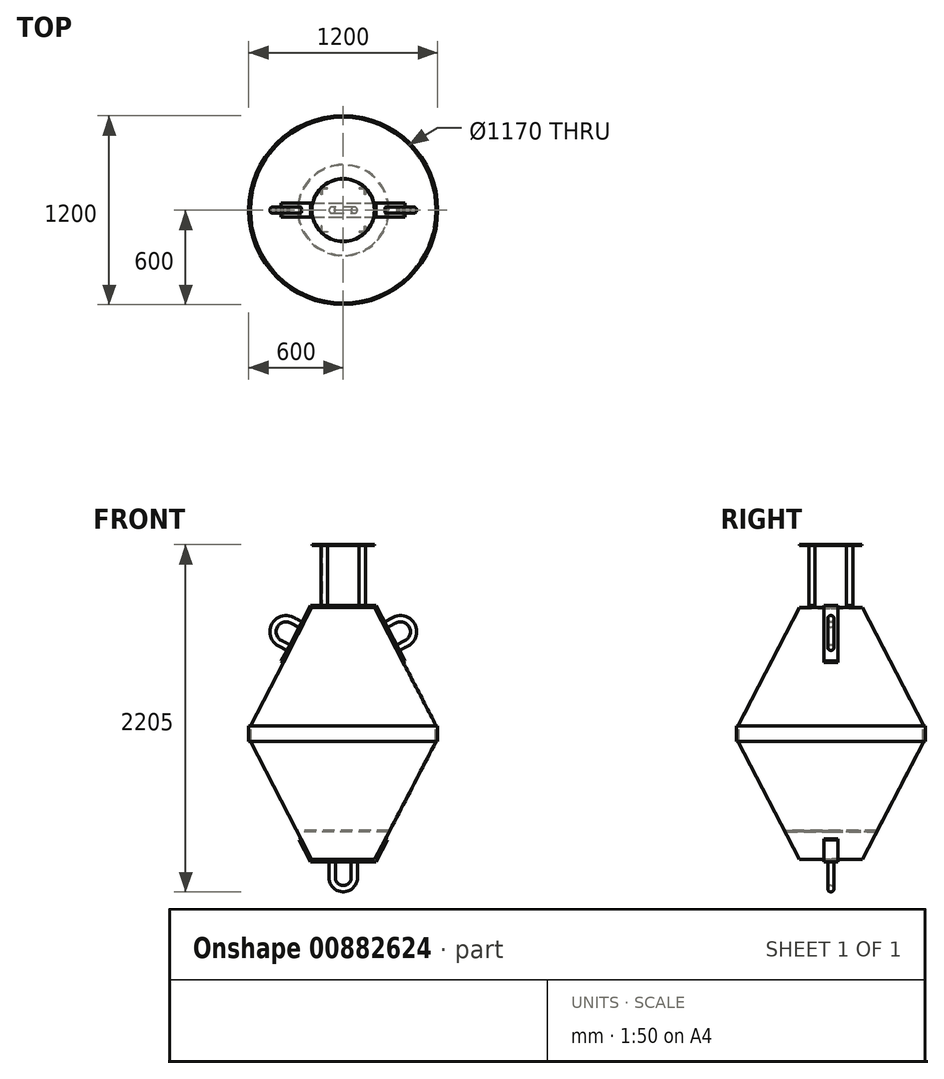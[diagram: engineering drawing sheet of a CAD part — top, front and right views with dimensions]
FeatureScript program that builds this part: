
annotation { "Feature Type Name" : "Feature", "Feature Type Description" : "" }
export const myFeature = defineFeature(function(context is Context, id is Id, definition is map)
    precondition{}
    {
        {
            var Q0;
            Q0=qCreatedBy(makeId("Front.planeOp"),FACE);
            var sketch = newSketch(context, id + "F0", { "sketchPlane" : qUnion([Q0])});
            skLineSegment(sketch, "E0", {"start": v(-100, 702.5) * mm, "end": v(290, -47.5) * mm});
            skLineSegment(sketch, "E1", {"start": v(290, -47.5) * mm, "end": v(300, -47.5) * mm});
            skLineSegment(sketch, "E2", {"start": v(300, -47.5) * mm, "end": v(300, -147.5) * mm});
            skLineSegment(sketch, "E3", {"start": v(300, -147.5) * mm, "end": v(290, -147.5) * mm});
            skLineSegment(sketch, "E4", {"start": v(290, -147.5) * mm, "end": v(-100, -897.5) * mm});
            skLineSegment(sketch, "E5", {"start": v(-100, -897.5) * mm, "end": v(-300, -897.5) * mm});
            skLineSegment(sketch, "E6", {"start": v(-300, -897.5) * mm, "end": v(-300, -892.5) * mm});
            skLineSegment(sketch, "E7", {"start": v(-300, -892.5) * mm, "end": v(-103.04, -892.5) * mm});
            skLineSegment(sketch, "E8", {"start": v(-103.04, -892.5) * mm, "end": v(-14.12, -721.5) * mm});
            skLineSegment(sketch, "E9", {"start": v(-14.12, -721.5) * mm, "end": v(-300, -721.5) * mm});
            skLineSegment(sketch, "E10", {"start": v(-300, -721.5) * mm, "end": v(-300, -713.5) * mm});
            skLineSegment(sketch, "E11", {"start": v(-300, -713.5) * mm, "end": v(-9.96, -713.5) * mm});
            skLineSegment(sketch, "E12", {"start": v(-9.96, -713.5) * mm, "end": v(285, -146.28) * mm});
            skLineSegment(sketch, "E13", {"start": v(285, -146.28) * mm, "end": v(285, -48.72) * mm});
            skLineSegment(sketch, "E14", {"start": v(285, -48.72) * mm, "end": v(-103.04, 697.5) * mm});
            skLineSegment(sketch, "E15", {"start": v(-103.04, 697.5) * mm, "end": v(-300, 697.5) * mm});
            skLineSegment(sketch, "E16", {"start": v(-300, 697.5) * mm, "end": v(-300, 702.5) * mm});
            skLineSegment(sketch, "E17", {"start": v(-300, 702.5) * mm, "end": v(-100, 702.5) * mm});
            skArc(sketch, "E18", {"start": v(-250, -1012.5) * mm, "mid": v(-264.64, -1047.86) * mm, "end": v(-300, -1062.5) * mm});
            skLineSegment(sketch, "E19", {"start": v(-300, -1062.5) * mm, "end": v(-300, -1102.5) * mm});
            skArc(sketch, "E20", {"start": v(-300, -1102.5) * mm, "mid": v(-236.36, -1076.14) * mm, "end": v(-210, -1012.5) * mm});
            skLineSegment(sketch, "E21", {"start": v(-210, -1012.5) * mm, "end": v(-210, -912.5) * mm});
            skLineSegment(sketch, "E22", {"start": v(-210, -912.5) * mm, "end": v(-250, -912.5) * mm});
            skLineSegment(sketch, "E23", {"start": v(-250, -912.5) * mm, "end": v(-250, -1012.5) * mm});
            skLineSegment(sketch, "E24", {"start": v(-300, 1102.5) * mm, "end": v(-160, 1102.5) * mm});
            skLineSegment(sketch, "E25", {"start": v(-160, 1102.5) * mm, "end": v(-160, 1097.5) * mm});
            skLineSegment(sketch, "E26", {"start": v(-160, 1097.5) * mm, "end": v(-300, 1097.5) * mm});
            skLineSegment(sketch, "E27", {"start": v(-300, 1097.5) * mm, "end": v(-300, 1102.5) * mm});
            skLineSegment(sketch, "E28", {"start": v(-200, 717.5) * mm, "end": v(-160, 717.5) * mm});
            skLineSegment(sketch, "E29", {"start": v(-160, 717.5) * mm, "end": v(-160, 1097.5) * mm});
            skLineSegment(sketch, "E30", {"start": v(-160, 1097.5) * mm, "end": v(-200, 1097.5) * mm});
            skLineSegment(sketch, "E31", {"start": v(-200, 1097.5) * mm, "end": v(-200, 717.5) * mm});
            skLineSegment(sketch, "E32", {"start": v(-90.9, 717.5) * mm, "end": v(93.65, 362.61) * mm});
            skLineSegment(sketch, "E33", {"start": v(93.65, 362.61) * mm, "end": v(80.34, 355.7) * mm});
            skLineSegment(sketch, "E34", {"start": v(80.34, 355.7) * mm, "end": v(-100, 702.5) * mm});
            skLineSegment(sketch, "E35", {"start": v(-100, 702.5) * mm, "end": v(-300, 702.5) * mm});
            skLineSegment(sketch, "E36", {"start": v(-300, 702.5) * mm, "end": v(-300, 717.5) * mm});
            skLineSegment(sketch, "E37", {"start": v(-300, 717.5) * mm, "end": v(-90.9, 717.5) * mm});
            skLineSegment(sketch, "E38", {"start": v(-17.84, -772) * mm, "end": v(-31.14, -765.08) * mm});
            skLineSegment(sketch, "E39", {"start": v(-31.14, -765.08) * mm, "end": v(-100, -897.5) * mm});
            skLineSegment(sketch, "E40", {"start": v(-300, -897.5) * mm, "end": v(-300, -912.5) * mm});
            skLineSegment(sketch, "E41", {"start": v(-300, -912.5) * mm, "end": v(-90.9, -912.5) * mm});
            skLineSegment(sketch, "E42", {"start": v(-90.9, -912.5) * mm, "end": v(-17.84, -772) * mm});
            skLineSegment(sketch, "E43", {"start": v(-18.23, 577.76) * mm, "end": v(-36.68, 613.25) * mm});
            skLineSegment(sketch, "E44", {"start": v(-36.68, 613.25) * mm, "end": v(16.55, 640.93) * mm});
            skArc(sketch, "E45", {"start": v(16.55, 640.93) * mm, "mid": v(154.78, 597.28) * mm, "end": v(111.13, 459.05) * mm});
            skLineSegment(sketch, "E46", {"start": v(111.13, 459.05) * mm, "end": v(57.9, 431.37) * mm});
            skLineSegment(sketch, "E47", {"start": v(57.9, 431.37) * mm, "end": v(39.44, 466.86) * mm});
            skLineSegment(sketch, "E48", {"start": v(39.44, 466.86) * mm, "end": v(92.67, 494.54) * mm});
            skArc(sketch, "E49", {"start": v(92.67, 494.54) * mm, "mid": v(119.29, 578.83) * mm, "end": v(35, 605.44) * mm});
            skLineSegment(sketch, "E50", {"start": v(35, 605.44) * mm, "end": v(-18.23, 577.76) * mm});
            skLineSegment(sketch, "E51", {"start": v(-300, 1102.5) * mm, "end": v(-300, -1143.28) * mm, "construction": true});
            skLineSegment(sketch, "E52.MirrorCS", {"start": v(-440, 1102.5) * mm, "end": v(-440, 1097.5) * mm});
            skLineSegment(sketch, "E53.MirrorCS", {"start": v(-440, 1097.5) * mm, "end": v(-400, 1097.5) * mm});
            skLineSegment(sketch, "E54.MirrorCS", {"start": v(-900, -147.5) * mm, "end": v(-890, -147.5) * mm});
            skLineSegment(sketch, "E55.MirrorCS", {"start": v(-500, 702.5) * mm, "end": v(-300, 702.5) * mm});
            skLineSegment(sketch, "E56.MirrorCS", {"start": v(-890, -47.5) * mm, "end": v(-900, -47.5) * mm});
            skLineSegment(sketch, "E57.MirrorCS", {"start": v(-563.32, 613.25) * mm, "end": v(-616.55, 640.93) * mm});
            skLineSegment(sketch, "E58.MirrorCS", {"start": v(-582.16, -772) * mm, "end": v(-568.86, -765.08) * mm});
            skLineSegment(sketch, "E59.MirrorCS", {"start": v(-693.65, 362.61) * mm, "end": v(-680.34, 355.7) * mm});
            skLineSegment(sketch, "E60.MirrorCS", {"start": v(-581.77, 577.76) * mm, "end": v(-563.32, 613.25) * mm});
            skLineSegment(sketch, "E61.MirrorCS", {"start": v(-635, 605.44) * mm, "end": v(-581.77, 577.76) * mm});
            skLineSegment(sketch, "E62.MirrorCS", {"start": v(-300, 1102.5) * mm, "end": v(-440, 1102.5) * mm});
            skLineSegment(sketch, "E63.MirrorCS", {"start": v(-500, -897.5) * mm, "end": v(-300, -897.5) * mm});
            skLineSegment(sketch, "E64.MirrorCS", {"start": v(-496.96, 697.5) * mm, "end": v(-300, 697.5) * mm});
            skLineSegment(sketch, "E65.MirrorCS", {"start": v(-885, -146.28) * mm, "end": v(-885, -48.72) * mm});
            skLineSegment(sketch, "E66.MirrorCS", {"start": v(-390, -912.5) * mm, "end": v(-350, -912.5) * mm});
            skLineSegment(sketch, "E67.MirrorCS", {"start": v(-300, 717.5) * mm, "end": v(-509.1, 717.5) * mm});
            skLineSegment(sketch, "E68.MirrorCS", {"start": v(-300, 702.5) * mm, "end": v(-500, 702.5) * mm});
            skLineSegment(sketch, "E69.MirrorCS", {"start": v(-350, -912.5) * mm, "end": v(-350, -1012.5) * mm});
            skLineSegment(sketch, "E70.MirrorCS", {"start": v(-657.9, 431.37) * mm, "end": v(-639.44, 466.86) * mm});
            skLineSegment(sketch, "E71.MirrorCS", {"start": v(-639.44, 466.86) * mm, "end": v(-692.67, 494.54) * mm});
            skArc(sketch, "E72.MirrorCS", {"start": v(-350, -1012.5) * mm, "mid": v(-335.36, -1047.86) * mm, "end": v(-300, -1062.5) * mm});
            skLineSegment(sketch, "E73.MirrorCS", {"start": v(-400, 717.5) * mm, "end": v(-440, 717.5) * mm});
            skLineSegment(sketch, "E74.MirrorCS", {"start": v(-711.13, 459.05) * mm, "end": v(-657.9, 431.37) * mm});
            skLineSegment(sketch, "E75.MirrorCS", {"start": v(-440, 1097.5) * mm, "end": v(-300, 1097.5) * mm});
            skLineSegment(sketch, "E76.MirrorCS", {"start": v(-900, -47.5) * mm, "end": v(-900, -147.5) * mm});
            skLineSegment(sketch, "E77.MirrorCS", {"start": v(-680.34, 355.7) * mm, "end": v(-500, 702.5) * mm});
            skLineSegment(sketch, "E78.MirrorCS", {"start": v(-440, 717.5) * mm, "end": v(-440, 1097.5) * mm});
            skArc(sketch, "E79.MirrorCS", {"start": v(-616.55, 640.93) * mm, "mid": v(-754.78, 597.28) * mm, "end": v(-711.13, 459.05) * mm});
            skArc(sketch, "E80.MirrorCS", {"start": v(-300, -1102.5) * mm, "mid": v(-363.64, -1076.14) * mm, "end": v(-390, -1012.5) * mm});
            skLineSegment(sketch, "E81.MirrorCS", {"start": v(-590.04, -713.5) * mm, "end": v(-885, -146.28) * mm});
            skLineSegment(sketch, "E82.MirrorCS", {"start": v(-496.96, -892.5) * mm, "end": v(-585.88, -721.5) * mm});
            skLineSegment(sketch, "E83.MirrorCS", {"start": v(-300, -713.5) * mm, "end": v(-590.04, -713.5) * mm});
            skLineSegment(sketch, "E84.MirrorCS", {"start": v(-390, -1012.5) * mm, "end": v(-390, -912.5) * mm});
            skArc(sketch, "E85.MirrorCS", {"start": v(-692.67, 494.54) * mm, "mid": v(-719.29, 578.83) * mm, "end": v(-635, 605.44) * mm});
            skLineSegment(sketch, "E86.MirrorCS", {"start": v(-585.88, -721.5) * mm, "end": v(-300, -721.5) * mm});
            skLineSegment(sketch, "E87.MirrorCS", {"start": v(-890, -147.5) * mm, "end": v(-500, -897.5) * mm});
            skLineSegment(sketch, "E88.MirrorCS", {"start": v(-400, 1097.5) * mm, "end": v(-400, 717.5) * mm});
            skLineSegment(sketch, "E89.MirrorCS", {"start": v(-568.86, -765.08) * mm, "end": v(-500, -897.5) * mm});
            skLineSegment(sketch, "E90.MirrorCS", {"start": v(-885, -48.72) * mm, "end": v(-496.96, 697.5) * mm});
            skLineSegment(sketch, "E91.MirrorCS", {"start": v(-500, 702.5) * mm, "end": v(-890, -47.5) * mm});
            skLineSegment(sketch, "E92.MirrorCS", {"start": v(-300, -892.5) * mm, "end": v(-496.96, -892.5) * mm});
            skLineSegment(sketch, "E93.MirrorCS", {"start": v(-509.1, -912.5) * mm, "end": v(-582.16, -772) * mm});
            skLineSegment(sketch, "E94.MirrorCS", {"start": v(-300, -912.5) * mm, "end": v(-509.1, -912.5) * mm});
            skLineSegment(sketch, "E95.MirrorCS", {"start": v(-509.1, 717.5) * mm, "end": v(-693.65, 362.61) * mm});
            skPoint(sketch, "E96", {"position": v(-230, -912.5) * mm});
            skPoint(sketch, "E97", {"position": v(-370, -912.5) * mm});
            skLineSegment(sketch, "E98", {"start": v(-210, -1012.5) * mm, "end": v(-250, -1012.5) * mm, "construction": true});
            skLineSegment(sketch, "E99", {"start": v(-350, -1012.5) * mm, "end": v(-390, -1012.5) * mm, "construction": true});
            skPoint(sketch, "E100", {"position": v(-230, -1012.5) * mm});
            skPoint(sketch, "E101", {"position": v(-370, -1012.5) * mm});
            skLineSegment(sketch, "E102", {"start": v(-230, -912.5) * mm, "end": v(-230, -1012.5) * mm});
            skLineSegment(sketch, "E103", {"start": v(-370, -912.5) * mm, "end": v(-370, -1012.5) * mm});
            skArc(sketch, "E104.trimOffspring", {"start": v(-370, -1012.5) * mm, "mid": v(-300, -1082.5) * mm, "end": v(-230, -1012.5) * mm});
            skLineSegment(sketch, "E105", {"start": v(0, 0) * mm, "end": v(-300, 0) * mm, "construction": true});
            skLineSegment(sketch, "E106", {"start": v(-300, 0) * mm, "end": v(-300, 84.93) * mm, "construction": true});
            skSolve(sketch);
        }
        {
            var Q0;
            {var subQ8=sQuery(id+"F0.wireOp",EDGE,"E33");Q0=makeQuery(id+"F0.imprint","IMPRINT",FACE,{"disambiguationData":[TD([[makeQuery(id+"F0.imprint","IMPRINT",EDGE,{"derivedFrom":subQ8}),-1.0]])]});}
            var Q1;
            {var subQ7=sQuery(id+"F0.wireOp",EDGE,"E36");Q1=makeQuery(id+"F0.imprint","IMPRINT",FACE,{"disambiguationData":[TD([[makeQuery(id+"F0.imprint","IMPRINT",EDGE,{"derivedFrom":subQ7}),1.0]])]});}
            var Q2;
            Q2=makeQuery(id+"F0.imprint","IMPRINT",FACE,{"disambiguationData":[TD([[makeQuery(id+"F0.imprint","IMPRINT",EDGE,{"derivedFrom":sQuery(id+"F0.wireOp",EDGE,"E38")}),1.0]])]});
            var Q3;
            {var subQ0=sQuery(id+"F0.wireOp",EDGE,"E40");Q3=makeQuery(id+"F0.imprint","IMPRINT",FACE,{"disambiguationData":[TD([[makeQuery(id+"F0.imprint","IMPRINT",EDGE,{"derivedFrom":subQ0}),-1.0]])]});}
            extrude(context, id + "F1", {"entities" : qUnion([Q0, Q1, Q2, Q3]), "endBound" : BoundingType.SYMMETRIC, "depth" : 90 * mm, "offsetDistance" : 25 * mm});
        }
        {
            var Q0;
            Q0=makeQuery(id+"F1.opExtrude","SWEPT_FACE",FACE,{"disambiguationData":[OSD([sQuery(id+"F0.wireOp",EDGE,"E41"),sQuery(id+"F0.wireOp",EDGE,"E94.MirrorCS")])]});
            var sketch = newSketch(context, id + "F2", { "sketchPlane" : qUnion([Q0])});
            skPoint(sketch, "E107.0", {"position": v(-230, 0) * mm});
            skPoint(sketch, "E108.0", {"position": v(-370, 0) * mm});
            skPoint(sketch, "E109.0", {"position": v(-210, 0) * mm});
            skPoint(sketch, "E110.0", {"position": v(-390, 0) * mm});
            skPoint(sketch, "E111.0", {"position": v(-350, 0) * mm});
            skPoint(sketch, "E112.0", {"position": v(-250, 0) * mm});
            skCircle(sketch, "E113", {"center": v(-230, 0) * mm, "radius": 20 * mm});
            skCircle(sketch, "E114", {"center": v(-370, 0) * mm, "radius": 20 * mm});
            skSolve(sketch);
        }
        {
            var Q0;
            Q0=makeQuery(id+"F2.imprint","IMPRINT",FACE,{"disambiguationData":[TD([[makeQuery(id+"F2.imprint","IMPRINT",EDGE,{"derivedFrom":sQuery(id+"F2.wireOp",EDGE,"E113")}),1.0]])]});
            var Q1;
            Q1=makeQuery(id+"F2.imprint","IMPRINT",FACE,{"disambiguationData":[TD([[makeQuery(id+"F2.imprint","IMPRINT",EDGE,{"derivedFrom":sQuery(id+"F2.wireOp",EDGE,"E114")}),1.0]])]});
            extrude(context, id + "F3", {"entities" : qUnion([Q0, Q1]), "operationType" : NewBodyOperationType.ADD, "depth" : 100 * mm, "offsetDistance" : 25 * mm});
        }
        {
            var Q0;
            Q0=makeQuery(id+"F3.opExtrude","CAP_FACE",FACE,{"disambiguationData":[OSD([sQuery(id+"F2.wireOp",EDGE,"E113")])],"isStart":false});
            var sketch = newSketch(context, id + "F4", { "sketchPlane" : qUnion([Q0])});
            skPoint(sketch, "E115.0", {"position": v(-300, 0) * mm});
            skPoint(sketch, "E116.0", {"position": v(-230, 0) * mm});
            skPoint(sketch, "E117.0", {"position": v(-370, 0) * mm});
            skCircle(sketch, "E118.0", {"center": v(-230, 0) * mm, "radius": 20 * mm});
            skCircle(sketch, "E119.0", {"center": v(-370, 0) * mm, "radius": 20 * mm});
            skLineSegment(sketch, "E120", {"start": v(-230, 0) * mm, "end": v(-370, 0) * mm, "construction": true});
            skLineSegment(sketch, "E121", {"start": v(-300, 0) * mm, "end": v(-300, 154.14) * mm, "construction": true});
            skSolve(sketch);
        }
        {
            var Q0;
            Q0=makeQuery(id+"F4.imprint","IMPRINT",FACE,{"disambiguationData":[TD([[makeQuery(id+"F4.imprint","IMPRINT",EDGE,{"derivedFrom":sQuery(id+"F4.wireOp",EDGE,"E118.0")}),1.0]])]});
            var Q1;
            Q1=sQuery(id+"F4.wireOp",EDGE,"E121");
            revolve(context, id + "F5", {"operationType" : NewBodyOperationType.ADD, "surfaceOperationType" : NewSurfaceOperationType.NEW, "entities" : qUnion([Q0]), "axis" : qUnion([Q1]), "revolveType" : RevolveType.ONE_DIRECTION, "oppositeDirection" : true, "angle" : 180 * degree});
        }
        {
            var Q0;
            Q0=makeQuery(id+"F1.opExtrude","SWEPT_FACE",FACE,{"disambiguationData":[OSD([sQuery(id+"F0.wireOp",EDGE,"E95.MirrorCS")])]});
            var sketch = newSketch(context, id + "F6", { "sketchPlane" : qUnion([Q0])});
            skPoint(sketch, "E122.0", {"position": v(0, 119.2) * mm});
            skPoint(sketch, "E123.0", {"position": v(0, 79.2) * mm});
            skPoint(sketch, "E124.0", {"position": v(0, 244.2) * mm});
            skPoint(sketch, "E125.0", {"position": v(0, 284.2) * mm});
            skLineSegment(sketch, "E126", {"start": v(0, 244.2) * mm, "end": v(0, 284.2) * mm, "construction": true});
            skLineSegment(sketch, "E127", {"start": v(0, 119.2) * mm, "end": v(0, 79.2) * mm, "construction": true});
            skPoint(sketch, "E128", {"position": v(0, 99.2) * mm});
            skPoint(sketch, "E129", {"position": v(0, 264.2) * mm});
            skCircle(sketch, "E130", {"center": v(0, 99.2) * mm, "radius": 20 * mm});
            skCircle(sketch, "E131", {"center": v(0, 264.2) * mm, "radius": 20 * mm});
            skSolve(sketch);
        }
        {
            var Q0;
            Q0=makeQuery(id+"F6.imprint","IMPRINT",FACE,{"disambiguationData":[TD([[makeQuery(id+"F6.imprint","IMPRINT",EDGE,{"derivedFrom":sQuery(id+"F6.wireOp",EDGE,"E131")}),1.0]])]});
            var Q1;
            Q1=makeQuery(id+"F6.imprint","IMPRINT",FACE,{"disambiguationData":[TD([[makeQuery(id+"F6.imprint","IMPRINT",EDGE,{"derivedFrom":sQuery(id+"F6.wireOp",EDGE,"E130")}),1.0]])]});
            extrude(context, id + "F7", {"entities" : qUnion([Q0, Q1]), "operationType" : NewBodyOperationType.ADD, "depth" : 60 * mm, "offsetDistance" : 25 * mm});
        }
        {
            var Q0;
            Q0=makeQuery(id+"F7.opExtrude","CAP_FACE",FACE,{"disambiguationData":[OSD([sQuery(id+"F6.wireOp",EDGE,"E131")])],"isStart":false});
            var sketch = newSketch(context, id + "F8", { "sketchPlane" : qUnion([Q0])});
            skPoint(sketch, "E132.0", {"position": v(0, 264.2) * mm});
            skCircle(sketch, "E133.0", {"center": v(0, 264.2) * mm, "radius": 20 * mm});
            skPoint(sketch, "E134.0", {"position": v(0, 99.2) * mm});
            skCircle(sketch, "E135.0", {"center": v(0, 99.2) * mm, "radius": 20 * mm});
            skLineSegment(sketch, "E136", {"start": v(0, 264.2) * mm, "end": v(0, 99.2) * mm, "construction": true});
            skPoint(sketch, "E137", {"position": v(0, 181.7) * mm});
            skLineSegment(sketch, "E138", {"start": v(0, 181.7) * mm, "end": v(-87.37, 181.7) * mm});
            skSolve(sketch);
        }
        {
            var Q0;
            Q0=makeQuery(id+"F8.imprint","IMPRINT",FACE,{"disambiguationData":[TD([[makeQuery(id+"F8.imprint","IMPRINT",EDGE,{"derivedFrom":sQuery(id+"F8.wireOp",EDGE,"E133.0")}),1.0]])]});
            var Q1;
            Q1=sQuery(id+"F8.wireOp",EDGE,"E138");
            revolve(context, id + "F9", {"operationType" : NewBodyOperationType.ADD, "surfaceOperationType" : NewSurfaceOperationType.NEW, "entities" : qUnion([Q0]), "axis" : qUnion([Q1]), "revolveType" : RevolveType.ONE_DIRECTION, "oppositeDirection" : true, "angle" : 180 * degree});
        }
        {
            var Q0;
            {var subQ0=sQuery(id+"F0.wireOp",EDGE,"E32");Q0=makeQuery(id+"F1.opExtrude","SWEPT_FACE",FACE,{"disambiguationData":[OSD([subQ0]),TDD([makeQuery(id+"F0.imprint","IMPRINT",EDGE,{"disambiguationData":[TD([[makeQuery(id+"F0.imprint","INTERSECT",VERTEX,{"derivedFrom":[subQ0,sQuery(id+"F0.wireOp",EDGE,"E43"),sQuery(id+"F0.wireOp",EDGE,"E50")]}),-1.0]])],"derivedFrom":subQ0})])]});}
            var sketch = newSketch(context, id + "F10", { "sketchPlane" : qUnion([Q0])});
            skPoint(sketch, "E139.0", {"position": v(0, 521.01) * mm});
            skPoint(sketch, "E140.0", {"position": v(0, 561.01) * mm});
            skPoint(sketch, "E141.0", {"position": v(0, 356.01) * mm});
            skPoint(sketch, "E142.0", {"position": v(0, 396.01) * mm});
            skLineSegment(sketch, "E143", {"start": v(0, 561.01) * mm, "end": v(0, 521.01) * mm, "construction": true});
            skLineSegment(sketch, "E144", {"start": v(0, 396.01) * mm, "end": v(0, 356.01) * mm, "construction": true});
            skPoint(sketch, "E145", {"position": v(0, 541.01) * mm});
            skPoint(sketch, "E146", {"position": v(0, 376.01) * mm});
            skCircle(sketch, "E147", {"center": v(0, 541.01) * mm, "radius": 20 * mm});
            skCircle(sketch, "E148", {"center": v(0, 376.01) * mm, "radius": 20 * mm});
            skSolve(sketch);
        }
        {
            var Q0;
            Q0=qSketchRegion(id+"F10",true);
            extrude(context, id + "F11", {"entities" : qUnion([Q0]), "operationType" : NewBodyOperationType.ADD, "depth" : 60 * mm, "offsetDistance" : 25 * mm});
        }
        {
            var Q0;
            Q0=makeQuery(id+"F11.opExtrude","CAP_FACE",FACE,{"disambiguationData":[OSD([sQuery(id+"F10.wireOp",EDGE,"E148")])],"isStart":false});
            var sketch = newSketch(context, id + "F12", { "sketchPlane" : qUnion([Q0])});
            skCircle(sketch, "E149.0.0", {"center": v(0, 376.01) * mm, "radius": 20 * mm});
            skCircle(sketch, "E150.0.0", {"center": v(0, 541.01) * mm, "radius": 20 * mm});
            skLineSegment(sketch, "E151", {"start": v(0, 541.01) * mm, "end": v(0, 376.01) * mm, "construction": true});
            skPoint(sketch, "E152", {"position": v(0, 458.51) * mm});
            skLineSegment(sketch, "E153", {"start": v(0, 458.51) * mm, "end": v(-58.6, 458.51) * mm, "construction": true});
            skSolve(sketch);
        }
        {
            var Q0;
            Q0=makeQuery(id+"F12.imprint","IMPRINT",FACE,{"disambiguationData":[TD([[makeQuery(id+"F12.imprint","IMPRINT",EDGE,{"derivedFrom":sQuery(id+"F12.wireOp",EDGE,"E150.0.0")}),1.0]])]});
            var Q1;
            Q1=sQuery(id+"F12.wireOp",EDGE,"E153");
            revolve(context, id + "F13", {"operationType" : NewBodyOperationType.ADD, "surfaceOperationType" : NewSurfaceOperationType.NEW, "entities" : qUnion([Q0]), "axis" : qUnion([Q1]), "revolveType" : RevolveType.ONE_DIRECTION, "oppositeDirection" : true, "angle" : 180 * degree});
        }
        {
            var Q0;
            Q0=makeQuery(id+"F1.opExtrude","SWEPT_FACE",FACE,{"disambiguationData":[OSD([sQuery(id+"F0.wireOp",EDGE,"E37"),sQuery(id+"F0.wireOp",EDGE,"E67.MirrorCS"),sQuery(id+"F0.wireOp",EDGE,"E73.MirrorCS")])]});
            var sketch = newSketch(context, id + "F14", { "sketchPlane" : qUnion([Q0])});
            skPoint(sketch, "E154.0", {"position": v(-160, 0) * mm});
            skPoint(sketch, "E155.0", {"position": v(-440, 0) * mm});
            skPoint(sketch, "E156.0", {"position": v(-400, 0) * mm});
            skPoint(sketch, "E157.0", {"position": v(-200, 0) * mm});
            skLineSegment(sketch, "E158", {"start": v(-160, 0) * mm, "end": v(-440, 0) * mm, "construction": true});
            skPoint(sketch, "E159", {"position": v(-300, 0) * mm});
            skLineSegment(sketch, "E160.bottom", {"start": v(-160, 140) * mm, "end": v(-440, 140) * mm, "construction": true});
            skLineSegment(sketch, "E160.top", {"start": v(-160, -140) * mm, "end": v(-440, -140) * mm, "construction": true});
            skLineSegment(sketch, "E160.left", {"start": v(-160, 140) * mm, "end": v(-160, -140) * mm, "construction": true});
            skLineSegment(sketch, "E160.right", {"start": v(-440, 140) * mm, "end": v(-440, -140) * mm, "construction": true});
            skLineSegment(sketch, "E161.bottom", {"start": v(-160, 140) * mm, "end": v(-200, 140) * mm});
            skLineSegment(sketch, "E161.top", {"start": v(-160, 100) * mm, "end": v(-164, 100) * mm});
            skLineSegment(sketch, "E161.left", {"start": v(-160, 140) * mm, "end": v(-160, 100) * mm});
            skLineSegment(sketch, "E161.right", {"start": v(-200, 140) * mm, "end": v(-200, 136) * mm});
            skLineSegment(sketch, "E162.top", {"start": v(-200, 136) * mm, "end": v(-164, 136) * mm});
            skLineSegment(sketch, "E162.right", {"start": v(-164, 100) * mm, "end": v(-164, 136) * mm});
            skSolve(sketch);
        }
        {
            var Q0;
            Q0=makeQuery(id+"F14.imprint","IMPRINT",FACE,{"disambiguationData":[TD([[makeQuery(id+"F14.imprint","IMPRINT",EDGE,{"derivedFrom":sQuery(id+"F14.wireOp",EDGE,"E161.bottom")}),1.0]])]});
            extrude(context, id + "F15", {"entities" : qUnion([Q0]), "depth" : 380 * mm, "offsetDistance" : 25 * mm});
        }
        {
            var Q0;
            Q0=makeQuery(id+"F15.opExtrude","SWEPT_BODY",BODY,{"disambiguationData":[OSD([sQuery(id+"F14.wireOp",EDGE,"E161.bottom"),sQuery(id+"F14.wireOp",EDGE,"E161.top"),sQuery(id+"F14.wireOp",EDGE,"E161.left"),sQuery(id+"F14.wireOp",EDGE,"E161.right"),sQuery(id+"F14.wireOp",EDGE,"E162.top"),sQuery(id+"F14.wireOp",EDGE,"E162.right")])]});
            var Q1;
            Q1=sQuery(id+"F0.wireOp",EDGE,"E51");
            circularPattern(context, id + "F16", {"entities" : qUnion([Q0]), "axis" : qUnion([Q1]), "angle" : 360 * degree, "instanceCount" : 4, "equalSpace" : true});
        }
        {
            var Q0;
            Q0=makeQuery(id+"F15.opExtrude","CAP_FACE",FACE,{"disambiguationData":[OSD([sQuery(id+"F14.wireOp",EDGE,"E161.bottom"),sQuery(id+"F14.wireOp",EDGE,"E161.top"),sQuery(id+"F14.wireOp",EDGE,"E161.left"),sQuery(id+"F14.wireOp",EDGE,"E161.right"),sQuery(id+"F14.wireOp",EDGE,"E162.top"),sQuery(id+"F14.wireOp",EDGE,"E162.right")])],"isStart":false});
            var sketch = newSketch(context, id + "F17", { "sketchPlane" : qUnion([Q0])});
            skPoint(sketch, "E163.0", {"position": v(-300, 0) * mm});
            skPoint(sketch, "E164.0", {"position": v(-160, 140) * mm});
            skCircle(sketch, "E165", {"center": v(-300, 0) * mm, "radius": 197.99 * mm});
            skSolve(sketch);
        }
        {
            var Q0;
            Q0=qSketchRegion(id+"F17",true);
            extrude(context, id + "F18", {"entities" : qUnion([Q0]), "depth" : 5 * mm, "offsetDistance" : 25 * mm});
        }
        {
            var Q0;
            Q0=makeQuery(id+"F0.imprint","IMPRINT",FACE,{"disambiguationData":[TD([[makeQuery(id+"F0.imprint","IMPRINT",EDGE,{"derivedFrom":sQuery(id+"F0.wireOp",EDGE,"E0")}),-1.0]])]});
            var Q1;
            Q1=sQuery(id+"F0.wireOp",EDGE,"E51");
            revolve(context, id + "F19", {"surfaceOperationType" : NewSurfaceOperationType.NEW, "entities" : qUnion([Q0]), "axis" : qUnion([Q1]), "revolveType" : RevolveType.FULL});
        }
        {
            var Q0;
            Q0=makeQuery(id+"F15.opExtrude","CAP_FACE",FACE,{"disambiguationData":[OSD([sQuery(id+"F14.wireOp",EDGE,"E161.bottom"),sQuery(id+"F14.wireOp",EDGE,"E161.top"),sQuery(id+"F14.wireOp",EDGE,"E161.left"),sQuery(id+"F14.wireOp",EDGE,"E161.right"),sQuery(id+"F14.wireOp",EDGE,"E162.top"),sQuery(id+"F14.wireOp",EDGE,"E162.right")])],"isStart":true});
            var Q1;
            Q1=makeQuery(id+"F16.opPattern","COPY",FACE,{"derivedFrom":makeQuery(id+"F15.opExtrude","CAP_FACE",FACE,{"disambiguationData":[OSD([sQuery(id+"F14.wireOp",EDGE,"E161.bottom"),sQuery(id+"F14.wireOp",EDGE,"E161.top"),sQuery(id+"F14.wireOp",EDGE,"E161.left"),sQuery(id+"F14.wireOp",EDGE,"E161.right"),sQuery(id+"F14.wireOp",EDGE,"E162.top"),sQuery(id+"F14.wireOp",EDGE,"E162.right")])],"isStart":true}),"instanceName":"3"});
            var Q2;
            Q2=makeQuery(id+"F16.opPattern","COPY",FACE,{"derivedFrom":makeQuery(id+"F15.opExtrude","CAP_FACE",FACE,{"disambiguationData":[OSD([sQuery(id+"F14.wireOp",EDGE,"E161.bottom"),sQuery(id+"F14.wireOp",EDGE,"E161.top"),sQuery(id+"F14.wireOp",EDGE,"E161.left"),sQuery(id+"F14.wireOp",EDGE,"E161.right"),sQuery(id+"F14.wireOp",EDGE,"E162.top"),sQuery(id+"F14.wireOp",EDGE,"E162.right")])],"isStart":true}),"instanceName":"2"});
            var Q3;
            Q3=makeQuery(id+"F16.opPattern","COPY",FACE,{"derivedFrom":makeQuery(id+"F15.opExtrude","CAP_FACE",FACE,{"disambiguationData":[OSD([sQuery(id+"F14.wireOp",EDGE,"E161.bottom"),sQuery(id+"F14.wireOp",EDGE,"E161.top"),sQuery(id+"F14.wireOp",EDGE,"E161.left"),sQuery(id+"F14.wireOp",EDGE,"E161.right"),sQuery(id+"F14.wireOp",EDGE,"E162.top"),sQuery(id+"F14.wireOp",EDGE,"E162.right")])],"isStart":true}),"instanceName":"1"});
            extrude(context, id + "F20", {"entities" : qUnion([Q0, Q1, Q2, Q3]), "endBound" : BoundingType.UP_TO_NEXT, "depth" : 25 * mm, "offsetDistance" : 25 * mm});
        }
    });
